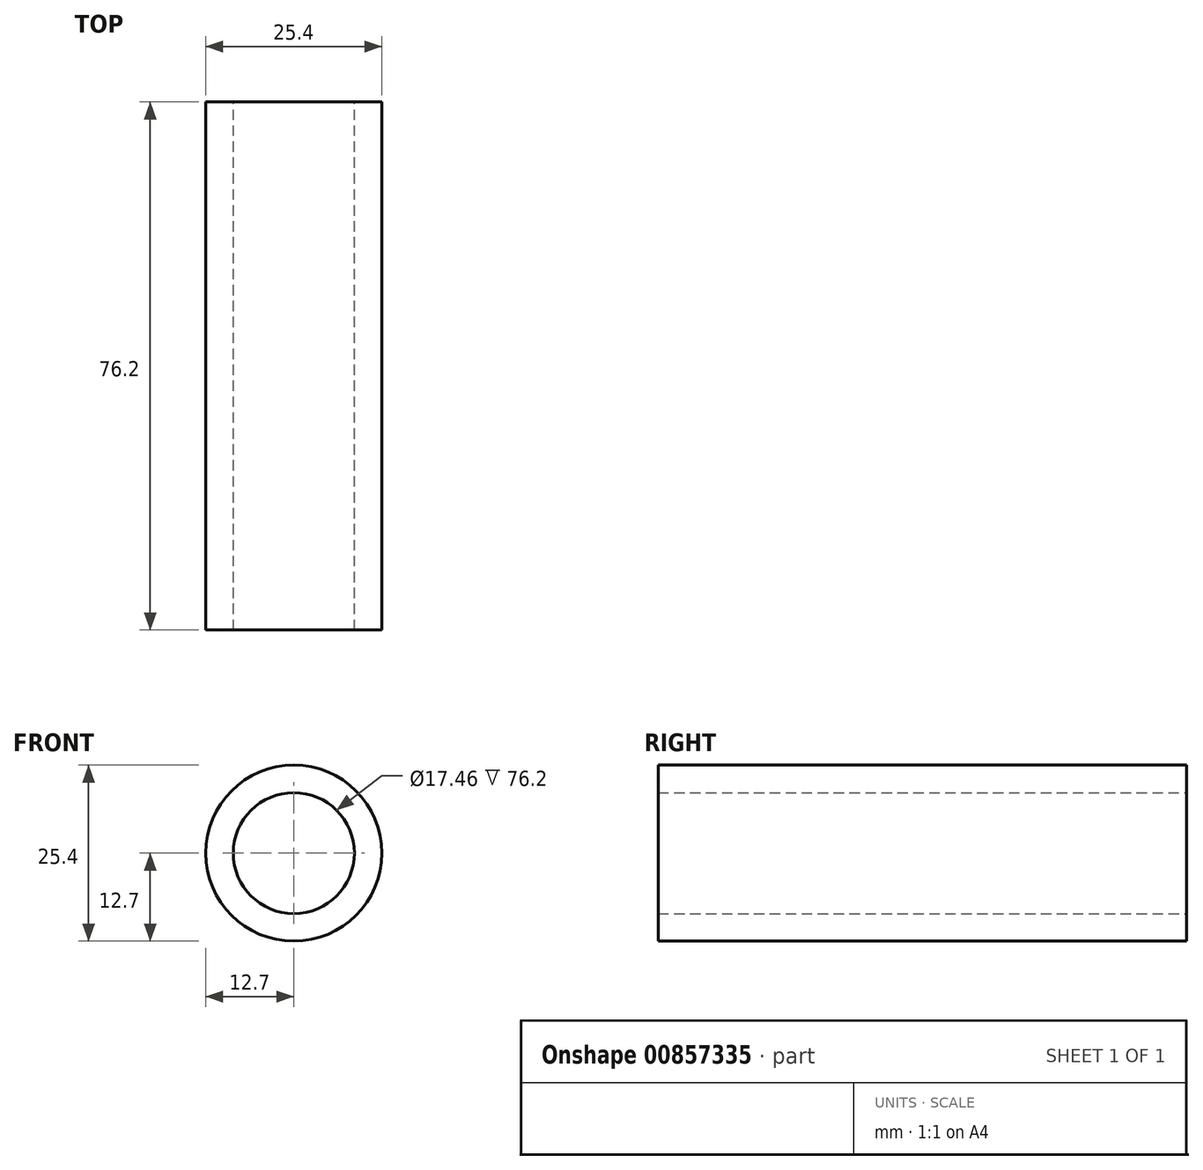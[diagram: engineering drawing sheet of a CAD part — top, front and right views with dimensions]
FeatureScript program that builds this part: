
annotation { "Feature Type Name" : "Feature", "Feature Type Description" : "" }
export const myFeature = defineFeature(function(context is Context, id is Id, definition is map)
    precondition{}
    {
        {
            var Q0;
            Q0=qCreatedBy(makeId("Front.planeOp"),FACE);
            var sketch = newSketch(context, id + "F0", { "sketchPlane" : qUnion([Q0])});
            skCircle(sketch, "E0", {"center": v(0, 0) * mm, "radius": 12.7 * mm});
            skCircle(sketch, "E1", {"center": v(0, 0) * mm, "radius": 8.73 * mm});
            skSolve(sketch);
        }
        {
            var Q0;
            Q0=makeQuery(id+"F0.imprint","IMPRINT",FACE,{"disambiguationData":[TD([[makeQuery(id+"F0.imprint","IMPRINT",EDGE,{"derivedFrom":sQuery(id+"F0.wireOp",EDGE,"E0")}),1.0]])]});
            extrude(context, id + "F1", {"entities" : qUnion([Q0]), "depth" : 76.2 * mm, "offsetDistance" : 25.4 * mm});
        }
    });
